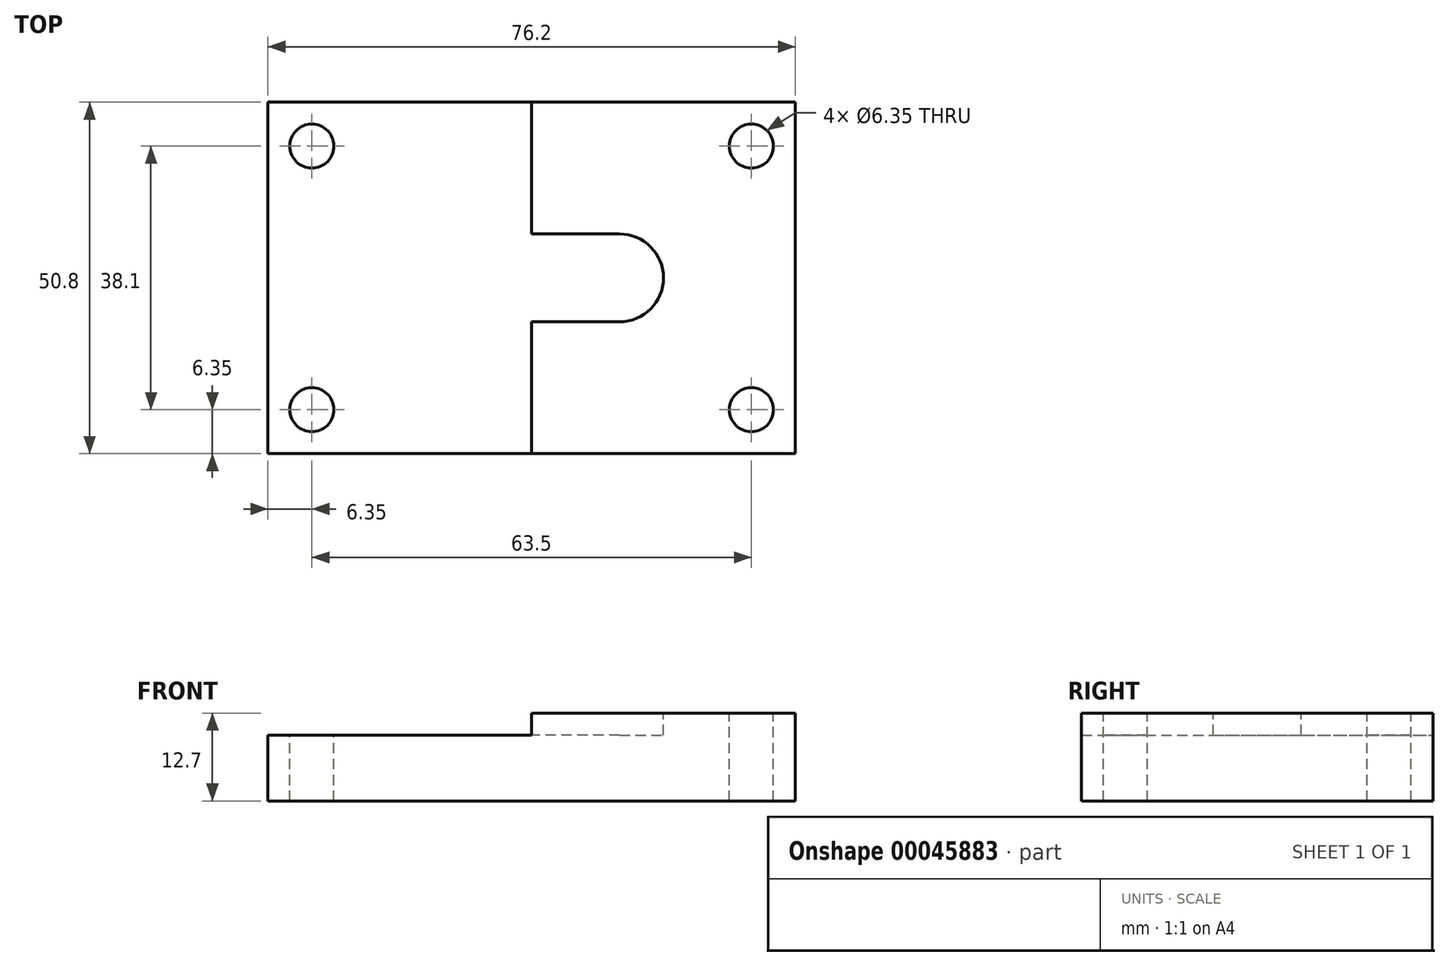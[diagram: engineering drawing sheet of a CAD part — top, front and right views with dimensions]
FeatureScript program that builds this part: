
annotation { "Feature Type Name" : "Feature", "Feature Type Description" : "" }
export const myFeature = defineFeature(function(context is Context, id is Id, definition is map)
    precondition{}
    {
        {
            var Q0;
            Q0=qCreatedBy(makeId("Top.planeOp"),FACE);
            var sketch = newSketch(context, id + "F0", { "sketchPlane" : qUnion([Q0])});
            skLineSegment(sketch, "E0.rect.bottom", {"start": v(-38.1, 25.4) * mm, "end": v(38.1, 25.4) * mm});
            skLineSegment(sketch, "E0.rect.top", {"start": v(-38.1, -25.4) * mm, "end": v(38.1, -25.4) * mm});
            skLineSegment(sketch, "E0.rect.left", {"start": v(-38.1, 25.4) * mm, "end": v(-38.1, -25.4) * mm});
            skLineSegment(sketch, "E0.rect.right", {"start": v(38.1, 25.4) * mm, "end": v(38.1, -25.4) * mm});
            skPoint(sketch, "E0.rect.middle", {"position": v(0, 0) * mm});
            skSolve(sketch);
        }
        {
            var Q0;
            Q0=makeQuery(id+"F0.imprint","IMPRINT",FACE,{"disambiguationData":[TD([[makeQuery(id+"F0.imprint","IMPRINT",EDGE,{"derivedFrom":sQuery(id+"F0.wireOp",EDGE,"E0.rect.bottom")}),-1.0]])]});
            extrude(context, id + "F1", {"entities" : qUnion([Q0]), "depth" : 12.7 * mm});
        }
        {
            var Q0;
            Q0=makeQuery(id+"F1.opExtrude","CAP_FACE",FACE,{"disambiguationData":[OSD([sQuery(id+"F0.wireOp",EDGE,"E0.rect.bottom"),sQuery(id+"F0.wireOp",EDGE,"E0.rect.top"),sQuery(id+"F0.wireOp",EDGE,"E0.rect.left"),sQuery(id+"F0.wireOp",EDGE,"E0.rect.right")])],"isStart":false});
            var sketch = newSketch(context, id + "F2", { "sketchPlane" : qUnion([Q0])});
            skCircle(sketch, "E1", {"center": v(-31.75, 19.05) * mm, "radius": 3.18 * mm});
            skCircle(sketch, "E2", {"center": v(-31.75, -19.05) * mm, "radius": 3.18 * mm});
            skCircle(sketch, "E3", {"center": v(31.75, 19.05) * mm, "radius": 3.18 * mm});
            skCircle(sketch, "E4", {"center": v(31.75, -19.05) * mm, "radius": 3.18 * mm});
            skSolve(sketch);
        }
        {
            var Q0;
            Q0=makeQuery(id+"F2.imprint","IMPRINT",FACE,{"disambiguationData":[TD([[makeQuery(id+"F2.imprint","IMPRINT",EDGE,{"derivedFrom":sQuery(id+"F2.wireOp",EDGE,"E1")}),1.0]])]});
            var Q1;
            Q1=makeQuery(id+"F2.imprint","IMPRINT",FACE,{"disambiguationData":[TD([[makeQuery(id+"F2.imprint","IMPRINT",EDGE,{"derivedFrom":sQuery(id+"F2.wireOp",EDGE,"E3")}),1.0]])]});
            var Q2;
            Q2=makeQuery(id+"F2.imprint","IMPRINT",FACE,{"disambiguationData":[TD([[makeQuery(id+"F2.imprint","IMPRINT",EDGE,{"derivedFrom":sQuery(id+"F2.wireOp",EDGE,"E4")}),1.0]])]});
            var Q3;
            Q3=makeQuery(id+"F2.imprint","IMPRINT",FACE,{"disambiguationData":[TD([[makeQuery(id+"F2.imprint","IMPRINT",EDGE,{"derivedFrom":sQuery(id+"F2.wireOp",EDGE,"E2")}),1.0]])]});
            extrude(context, id + "F3", {"entities" : qUnion([Q0, Q1, Q2, Q3]), "operationType" : NewBodyOperationType.REMOVE, "endBound" : BoundingType.THROUGH_ALL, "oppositeDirection" : true, "depth" : 25.4 * mm});
        }
        {
            var Q0;
            Q0=makeQuery(id+"F1.opExtrude","CAP_FACE",FACE,{"disambiguationData":[OSD([sQuery(id+"F0.wireOp",EDGE,"E0.rect.bottom"),sQuery(id+"F0.wireOp",EDGE,"E0.rect.top"),sQuery(id+"F0.wireOp",EDGE,"E0.rect.left"),sQuery(id+"F0.wireOp",EDGE,"E0.rect.right")])],"isStart":false});
            var sketch = newSketch(context, id + "F4", { "sketchPlane" : qUnion([Q0])});
            skLineSegment(sketch, "E5.rect.bottom", {"start": v(12.7, -6.35) * mm, "end": v(-12.7, -6.35) * mm});
            skLineSegment(sketch, "E5.rect.top", {"start": v(12.7, 6.35) * mm, "end": v(-12.7, 6.35) * mm});
            skLineSegment(sketch, "E5.rect.left", {"start": v(19.05, 0) * mm, "end": v(19.05, 0) * mm});
            skLineSegment(sketch, "E5.rect.right", {"start": v(-19.05, 0) * mm, "end": v(-19.05, 0) * mm});
            skPoint(sketch, "E5.rect.middle", {"position": v(0, 0) * mm});
            skPoint(sketch, "E6.visualSharp", {"position": v(19.05, 6.35) * mm});
            skArc(sketch, "E6.filletArc", {"start": v(19.05, 0) * mm, "mid": v(17.2, 4.5) * mm, "end": v(12.7, 6.35) * mm});
            skPoint(sketch, "E7.visualSharp", {"position": v(19.05, -6.35) * mm});
            skArc(sketch, "E7.filletArc", {"start": v(12.7, -6.35) * mm, "mid": v(17.2, -4.5) * mm, "end": v(19.05, 0) * mm});
            skPoint(sketch, "E8.visualSharp", {"position": v(-19.05, -6.35) * mm});
            skArc(sketch, "E8.filletArc", {"start": v(-19.05, 0) * mm, "mid": v(-17.2, -4.5) * mm, "end": v(-12.7, -6.35) * mm});
            skPoint(sketch, "E9.visualSharp", {"position": v(-19.05, 6.35) * mm});
            skArc(sketch, "E9.filletArc", {"start": v(-12.7, 6.35) * mm, "mid": v(-17.2, 4.5) * mm, "end": v(-19.05, 0) * mm});
            skSolve(sketch);
        }
        {
            var Q0;
            Q0=makeQuery(id+"F4.imprint","IMPRINT",FACE,{"disambiguationData":[TD([[makeQuery(id+"F4.imprint","IMPRINT",EDGE,{"derivedFrom":sQuery(id+"F4.wireOp",EDGE,"E5.rect.bottom")}),-1.0]])]});
            extrude(context, id + "F5", {"entities" : qUnion([Q0]), "operationType" : NewBodyOperationType.REMOVE, "oppositeDirection" : true, "depth" : 3.17 * mm});
        }
        {
            var Q0;
            Q0=makeQuery(id+"F1.opExtrude","CAP_FACE",FACE,{"disambiguationData":[OSD([sQuery(id+"F0.wireOp",EDGE,"E0.rect.bottom"),sQuery(id+"F0.wireOp",EDGE,"E0.rect.top"),sQuery(id+"F0.wireOp",EDGE,"E0.rect.left"),sQuery(id+"F0.wireOp",EDGE,"E0.rect.right")])],"isStart":false});
            var sketch = newSketch(context, id + "F6", { "sketchPlane" : qUnion([Q0])});
            skLineSegment(sketch, "E10.bottom", {"start": v(-38.1, 25.4) * mm, "end": v(0, 25.4) * mm});
            skLineSegment(sketch, "E10.top", {"start": v(-38.1, -25.4) * mm, "end": v(0, -25.4) * mm});
            skLineSegment(sketch, "E10.left", {"start": v(-38.1, 25.4) * mm, "end": v(-38.1, -25.4) * mm});
            skLineSegment(sketch, "E10.right", {"start": v(0, 25.4) * mm, "end": v(0, -25.4) * mm});
            skSolve(sketch);
        }
        {
            var Q0;
            {var subQ7=sQuery(id+"F6.wireOp",EDGE,"E10.bottom");Q0=makeQuery(id+"F6.imprint","IMPRINT",FACE,{"disambiguationData":[TD([[makeQuery(id+"F6.imprint","IMPRINT",EDGE,{"derivedFrom":subQ7}),-1.0]])]});}
            var Q1;
            Q1=makeQuery(id+"F5.boolean.opBoolean","COPY",FACE,{"derivedFrom":makeQuery(id+"F5.opExtrude","CAP_FACE",FACE,{"disambiguationData":[OSD([sQuery(id+"F4.wireOp",EDGE,"E5.rect.bottom"),sQuery(id+"F4.wireOp",EDGE,"E5.rect.top"),sQuery(id+"F4.wireOp",EDGE,"E6.filletArc"),sQuery(id+"F4.wireOp",EDGE,"E7.filletArc"),sQuery(id+"F4.wireOp",EDGE,"E8.filletArc"),sQuery(id+"F4.wireOp",EDGE,"E9.filletArc")])],"isStart":false})});
            extrude(context, id + "F7", {"entities" : qUnion([Q0]), "operationType" : NewBodyOperationType.REMOVE, "endBound" : BoundingType.UP_TO_SURFACE, "oppositeDirection" : true, "endBoundEntityFace" : qUnion([Q1]), "depth" : 25.4 * mm});
        }
    });
